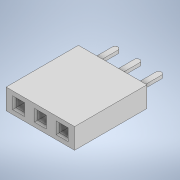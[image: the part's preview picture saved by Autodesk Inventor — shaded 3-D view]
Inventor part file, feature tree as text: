
AUTODESK INVENTOR PART (.ipt)
format: ipt  version: 2021 (Build 250183000, 183)  size: 173,056 bytes
history: native  units: mm
features: extrude x3, sketch x3, chamfer x1, projected_geometry x1
ambient origin geometry x8: Origin, YZ Plane, XZ Plane, XY Plane, X Axis, Y Axis, Z Axis, Center Point
bodies: Solid1 (feature_tree)
feature tree (8):
  extrude  "Extrusion1"  Depth=2.4mm
  extrude  "Extrusion2"  Depth=2.54mm
  extrude  "Extrusion3"  Depth=8.45mm TaperAngle=0.0deg
  chamfer  "Chamfer1"  Distance=1.0mm
  sketch  "Sketch1"  dims[d0=8.0mm d1=2.4mm]
  sketch  "Sketch2"  dims[d2=1.0mm d3=2.54mm]
  projected_geometry  "Projected Loop1"
  sketch  "Sketch3"  dims[d4=2.54mm d5=8.45mm d6=0.0mm d7=1.0mm d8=0.0mm d9=2.54mm d10=2.54mm d11=0.65mm d12=0.375mm d13=3.15mm d14=0.0mm d15=0.2mm d16=2.0mm d17=45.0deg]
